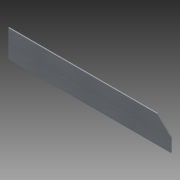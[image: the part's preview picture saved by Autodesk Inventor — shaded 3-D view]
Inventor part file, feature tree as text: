
AUTODESK INVENTOR PART (.ipt)
format: ipt  version: 2011 SP1 (Build 150282100, 282)  size: 77,312 bytes
history: native  units: in
note: dims shown in document units (in); Inventor stores cm internally (conversion verified against a paired STEP export)
features: extrude x1, sketch x1
ambient origin geometry x8: Origin, YZ Plane, XZ Plane, XY Plane, X Axis, Y Axis, Z Axis, Center Point
bodies: Solid1 (feature_tree)
feature tree (2):
  extrude  "Extrusion1"  Depth=1.5in
  sketch  "Sketch1"  dims[d1=3.0in d2=1.5in d3=9.0in d4=0.125in d5=0.0in d6=1.5in d7=45.0deg d8=18.0in]
